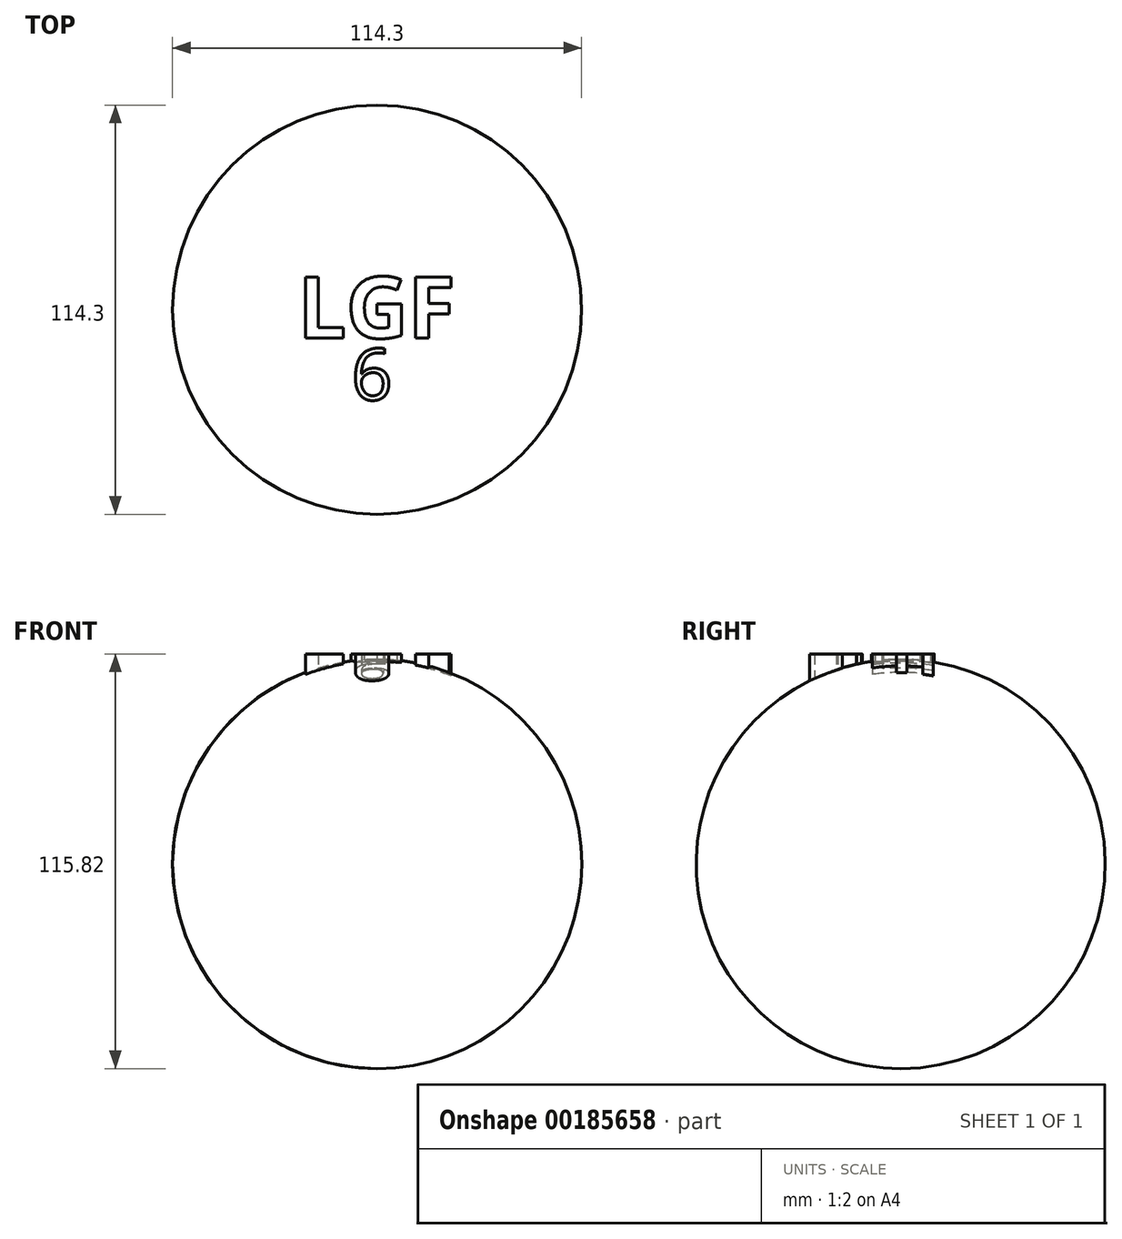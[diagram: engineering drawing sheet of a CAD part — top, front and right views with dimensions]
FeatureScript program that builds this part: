
annotation { "Feature Type Name" : "Feature", "Feature Type Description" : "" }
export const myFeature = defineFeature(function(context is Context, id is Id, definition is map)
    precondition{}
    {
        {
            var Q0;
            Q0=qCreatedBy(makeId("Front.planeOp"),FACE);
            var sketch = newSketch(context, id + "F0", { "sketchPlane" : qUnion([Q0])});
            skCircle(sketch, "E0", {"center": v(0, 0) * mm, "radius": 57.15 * mm});
            skLineSegment(sketch, "E1", {"start": v(0, 57.15) * mm, "end": v(0, -57.15) * mm});
            skSolve(sketch);
        }
        {
            var Q0;
            {var subQ0=sQuery(id+"F0.wireOp",EDGE,"E1");Q0=makeQuery(id+"F0.imprint","IMPRINT",FACE,{"disambiguationData":[TD([[makeQuery(id+"F0.imprint","IMPRINT",EDGE,{"derivedFrom":subQ0}),1.0]])]});}
            var Q1;
            Q1=sQuery(id+"F0.wireOp",EDGE,"E1");
            revolve(context, id + "F1", {"entities" : qUnion([Q0]), "axis" : qUnion([Q1]), "revolveType" : RevolveType.FULL});
        }
        {
            var Q0;
            Q0=qCreatedBy(makeId("Top.planeOp"),FACE);
            var sketch = newSketch(context, id + "F2", { "sketchPlane" : qUnion([Q0])});
            skText(sketch, "E2", { "text": "LGF", "fontName": "OpenSans-Bold.ttf"});
            skText(sketch, "E3", { "text": "6", "fontName": "OpenSans-Regular.ttf"});
            const initialGuessF2  = {"E2": [-0.0222, -0.00795, 1, 0, 0.01723], "E3": [-0.0072, -0.02523, 1, 0, 0.01441]};
            skSetInitialGuess(sketch, initialGuessF2);
            skSolve(sketch);
        }
        {
            var Q0;
            Q0 = qSketchRegion(id + "F2", true);
            extrude(context, id + "F3", {"entities" : qUnion([Q0]), "operationType" : NewBodyOperationType.ADD, "depth" : 25.4 * mm});
        }
        {
            var Q0;
            Q0 = qSketchRegion(id + "F2", true);
            extrude(context, id + "F4", {"entities" : qUnion([Q0]), "operationType" : NewBodyOperationType.ADD, "depth" : 58.67 * mm});
        }
    });
